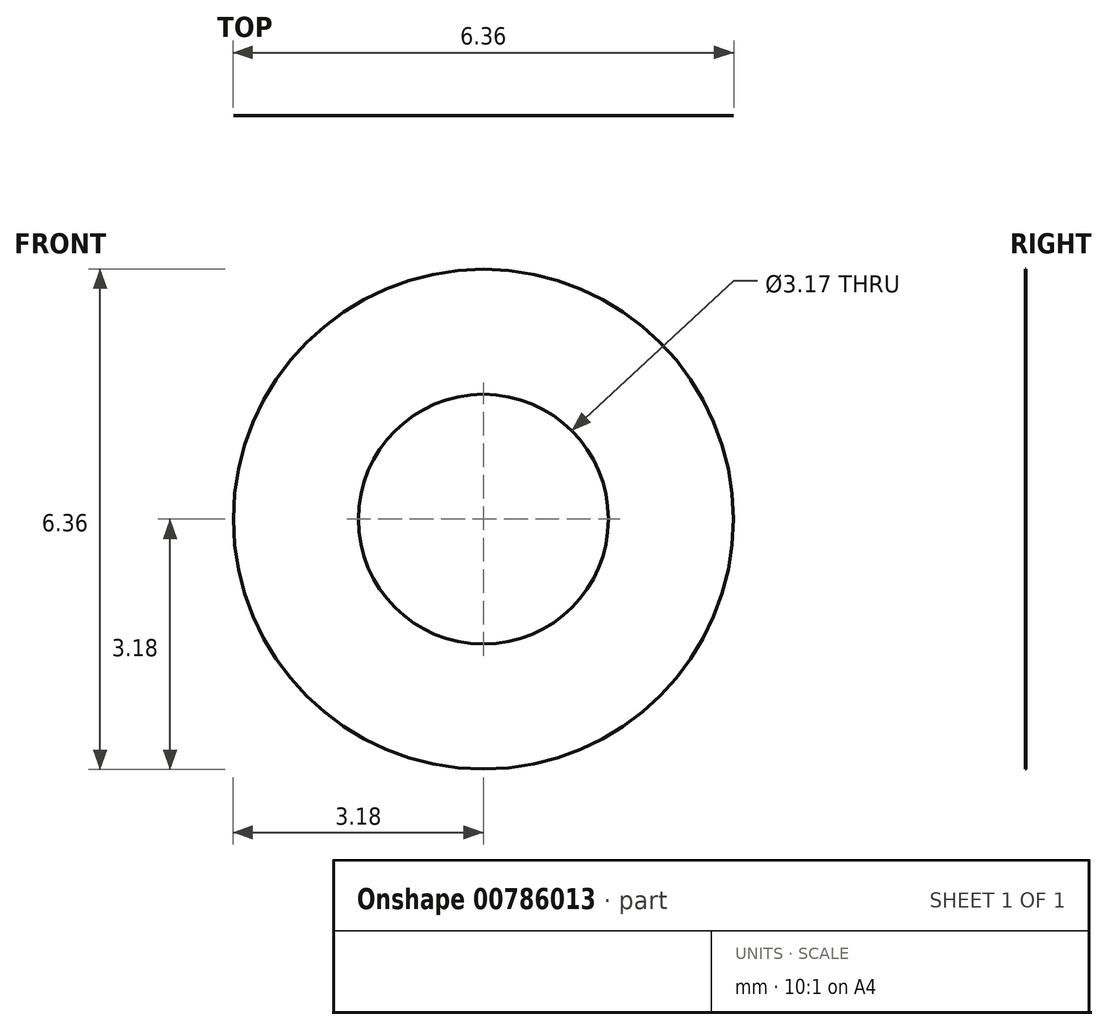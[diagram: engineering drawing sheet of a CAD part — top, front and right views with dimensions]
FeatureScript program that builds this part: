
annotation { "Feature Type Name" : "Feature", "Feature Type Description" : "" }
export const myFeature = defineFeature(function(context is Context, id is Id, definition is map)
    precondition{}
    {
        {
            var Q0;
            Q0=qCreatedBy(makeId("Front.planeOp"),FACE);
            var sketch = newSketch(context, id + "F0", { "sketchPlane" : qUnion([Q0])});
            skCircle(sketch, "E0", {"center": v(0, 0) * mm, "radius": 1.59 * mm});
            skCircle(sketch, "E1", {"center": v(0, 0) * mm, "radius": 3.18 * mm});
            skSolve(sketch);
        }
        {
            var Q0;
            Q0=qSketchRegion(id+"F0",true);
            extrude(context, id + "F1", {"entities" : qUnion([Q0]), "depth" : 1 / 203.2 * mm, "offsetDistance" : 25 * mm});
        }
    });
